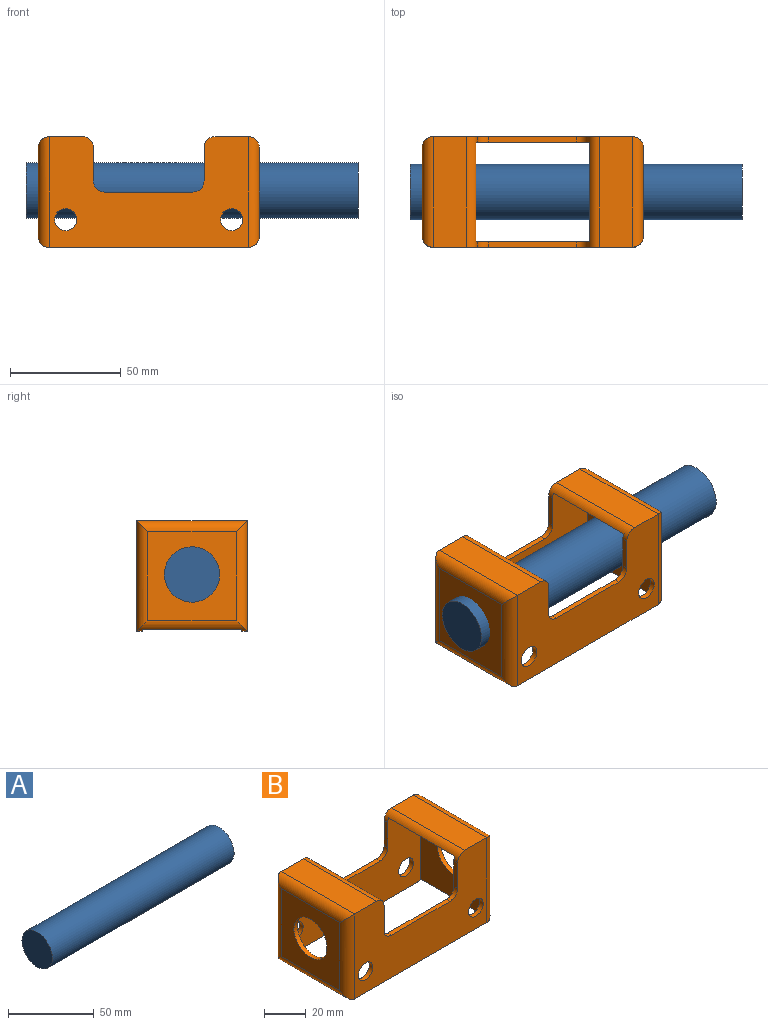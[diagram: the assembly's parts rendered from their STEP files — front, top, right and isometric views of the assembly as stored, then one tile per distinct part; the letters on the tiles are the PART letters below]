
ASSEMBLY  parts=2 mates=1
PART A: 3 faces, bbox 150x25x25 mm
  f0: cylinder r=12.5mm len=150mm, axis (1,0,0), area 11781mm2, adj f1,f2
  f1: plane 25x25mm, normal (-1,0,0), area 490.9mm2, adj f0
  f2: plane 25x25mm, normal (1,0,0), area 490.9mm2, adj f0
PART B: 40 faces, bbox 100x50x50 mm
  f0: plane 90x2.5mm, normal (0,0,-1), area 225mm2, adj f9,f14,f26,f36
  f1: plane 15x2.5mm, normal (-1,0,0), area 37.5mm2, adj f7,f12,f29,f30
  f2: plane 15x2.5mm, normal (1,0,0), area 37.5mm2, adj f9,f14,f31,f33
  f3: plane 50x15mm, normal (0,0,1), area 750mm2, adj f7,f9,f30,f35
  f4: plane 45x21.83mm, normal (0,0,-1), area 982.4mm2, adj f12,f13,f14,f30
  f5: plane 90x2.5mm, normal (0,0,-1), area 225mm2, adj f7,f12,f26,f36
  f6: plane 40x40mm, normal (-1,0,0), area 1202.4mm2, adj f24,f25,f26,f27,f39
  f7: plane 90x50mm, normal (0,-1,0), area 3092.9mm2, adj f1,f3,f5,f10,f16,f18,f22,f23
  f8: plane 40x40mm, normal (1,0,0), area 1202.4mm2, adj f34,f35,f36,f37,f38
  f9: plane 90x50mm, normal (0,1,0), area 3092.9mm2, adj f0,f2,f3,f10,f17,f19,f20,f21
  f10: plane 50x15mm, normal (0,0,1), area 750mm2, adj f7,f9,f25,f31
  f11: plane 46.83x45mm, normal (1,0,0), area 1709.7mm2, adj f12,f14,f15,f26,f39
  f12: plane 95x47.5mm, normal (0,1,0), area 3239mm2, adj f1,f4,f5,f11,f13,f15,f16,f18
  f13: plane 46.83x45mm, normal (-1,0,0), area 1709.7mm2, adj f4,f12,f14,f36,f38
  f14: plane 95x47.5mm, normal (0,-1,0), area 3239mm2, adj f0,f2,f4,f11,f13,f15,f17,f19
  f15: plane 45x21.83mm, normal (0,0,-1), area 982.4mm2, adj f11,f12,f14,f31
  f16: plane 40x2.5mm, normal (0,0,1), area 100mm2, adj f7,f12,f28,f29
  f17: plane 40x2.5mm, normal (0,0,1), area 100mm2, adj f9,f14,f32,f33
  f18: plane 15x2.5mm, normal (1,0,0), area 37.5mm2, adj f7,f12,f28,f31
  f19: plane 15x2.5mm, normal (-1,0,0), area 37.5mm2, adj f9,f14,f30,f32
  f20: cylinder r=5mm len=10mm, axis (0,-1,0), area 78.5mm2, adj f9,f14
  f21: cylinder r=5mm len=10mm, axis (0,-1,0), area 78.5mm2, adj f9,f14
  f22: cylinder r=5mm len=10mm, axis (0,-1,0), area 78.5mm2, adj f7,f12
  f23: cylinder r=5mm len=10mm, axis (0,-1,0), area 78.5mm2, adj f7,f12
  f24: cylinder r=5mm len=50mm, axis (0,0,-1), area 364.2mm2, adj f6,f9,f25,f26
  f25: cylinder r=5mm len=50mm, axis (0,1,0), area 364.2mm2, adj f6,f10,f24,f27
  f26: cylinder r=5mm len=50mm, axis (0,-1,0), area 246.3mm2, adj f0,f5,f6,f11,f12,f14,f24,f27
  f27: cylinder r=5mm len=50mm, axis (0,0,1), area 364.2mm2, adj f6,f7,f25,f26
  f28: cylinder r=5mm len=5mm, axis (0,-1,0), area 19.6mm2, adj f7,f12,f16,f18
  f29: cylinder r=5mm len=5mm, axis (0,1,0), area 19.6mm2, adj f1,f7,f12,f16
  f30: cylinder r=5mm len=50mm, axis (0,-1,0), area 274.9mm2, adj f1,f3,f4,f7,f9,f12,f14,f19
  f31: cylinder r=5mm len=50mm, axis (0,1,0), area 274.9mm2, adj f2,f7,f9,f10,f12,f14,f15,f18
  f32: cylinder r=5mm len=5mm, axis (0,1,0), area 19.6mm2, adj f9,f14,f17,f19
  f33: cylinder r=5mm len=5mm, axis (0,-1,0), area 19.6mm2, adj f2,f9,f14,f17
  f34: cylinder r=5mm len=50mm, axis (0,0,1), area 364.2mm2, adj f8,f9,f35,f36
  f35: cylinder r=5mm len=50mm, axis (0,-1,0), area 364.2mm2, adj f3,f8,f34,f37
  f36: cylinder r=5mm len=50mm, axis (0,1,0), area 246.3mm2, adj f0,f5,f8,f12,f13,f14,f34,f37
  f37: cylinder r=5mm len=50mm, axis (0,0,-1), area 364.2mm2, adj f7,f8,f35,f36
  f38: cylinder r=11.25mm len=22.5mm, axis (1,0,0), area 176.7mm2, adj f8,f13
  f39: cylinder r=11.25mm len=22.5mm, axis (1,0,0), area 176.7mm2, adj f6,f11
PLACE A rot(axis=(-1,0,0),45.6deg) t=(84.42,34.23,47.64)mm
PLACE B t=(-60.15,9.23,21.97)mm fixed
MATE cylindrical A.f0 <-> B.f38  axis (1,0,0) through (84.42,34.23,47.64)mm
